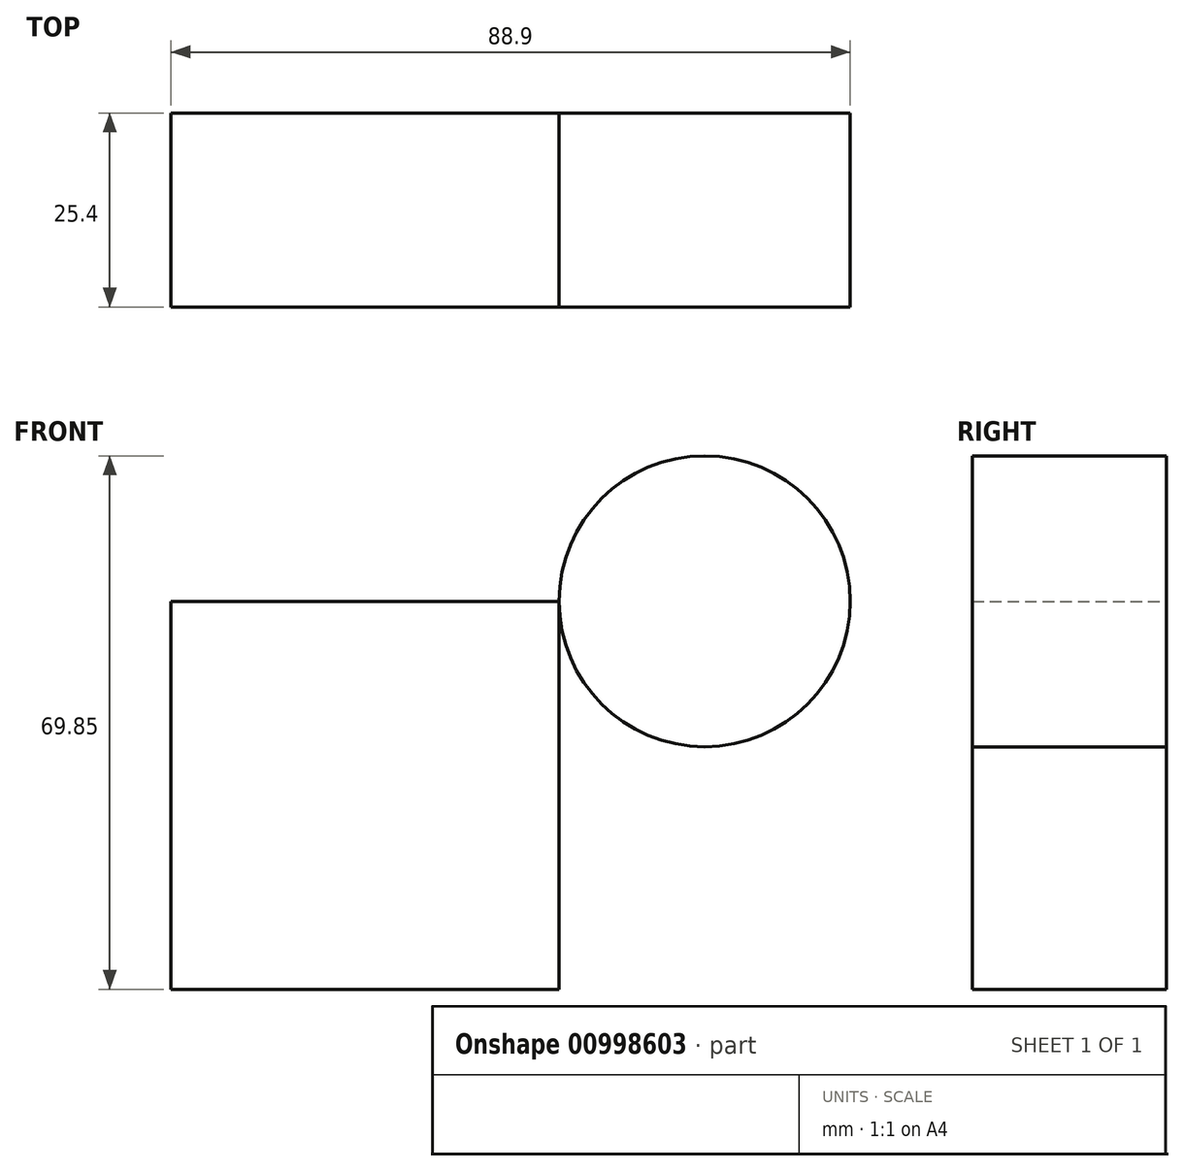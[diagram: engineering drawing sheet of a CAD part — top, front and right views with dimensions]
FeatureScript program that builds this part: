
annotation { "Feature Type Name" : "Feature", "Feature Type Description" : "" }
export const myFeature = defineFeature(function(context is Context, id is Id, definition is map)
    precondition{}
    {
        {
            var Q0;
            Q0=qCreatedBy(makeId("Front.planeOp"),FACE);
            var sketch = newSketch(context, id + "F0", { "sketchPlane" : qUnion([Q0])});
            skLineSegment(sketch, "E0.bottom", {"start": v(0, 0) * mm, "end": v(50.8, 0) * mm});
            skLineSegment(sketch, "E0.top", {"start": v(0, 50.8) * mm, "end": v(50.8, 50.8) * mm});
            skLineSegment(sketch, "E0.left", {"start": v(0, 0) * mm, "end": v(0, 50.8) * mm});
            skLineSegment(sketch, "E0.right", {"start": v(50.8, 0) * mm, "end": v(50.8, 50.8) * mm});
            skCircle(sketch, "E1", {"center": v(69.85, 50.8) * mm, "radius": 19.05 * mm});
            skLineSegment(sketch, "E2", {"start": v(25.4, 50.8) * mm, "end": v(25.4, 0) * mm, "construction": true});
            skLineSegment(sketch, "E3", {"start": v(0, 25.4) * mm, "end": v(50.8, 25.4) * mm, "construction": true});
            skSolve(sketch);
        }
        {
            var Q0;
            Q0 = qSketchRegion(id + "F0", true);
            extrude(context, id + "F1", {"entities" : qUnion([Q0]), "depth" : 25.4 * mm, "offsetDistance" : 25.4 * mm});
        }
    });
